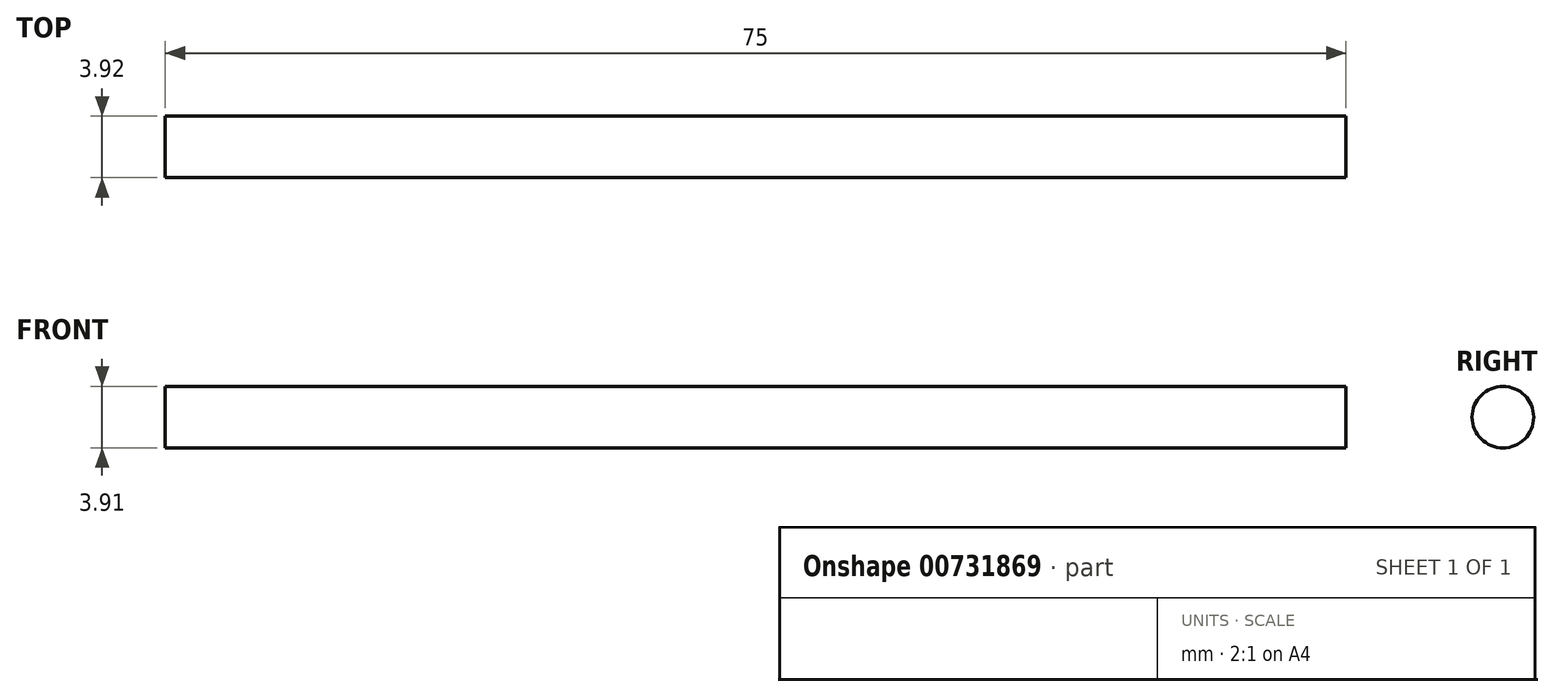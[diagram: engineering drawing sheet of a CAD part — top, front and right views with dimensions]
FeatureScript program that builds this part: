
annotation { "Feature Type Name" : "Feature", "Feature Type Description" : "" }
export const myFeature = defineFeature(function(context is Context, id is Id, definition is map)
    precondition{}
    {
        {
            var Q0;
            Q0=qCreatedBy(makeId("Right.planeOp"),FACE);
            var sketch = newSketch(context, id + "F0", { "sketchPlane" : qUnion([Q0])});
            skCircle(sketch, "E0", {"center": v(-4.15, 6.52) * mm, "radius": 1.96 * mm});
            skSolve(sketch);
        }
        {
            var Q0;
            Q0 = qSketchRegion(id + "F0", true);
            extrude(context, id + "F1", {"entities" : qUnion([Q0]), "depth" : 75 * mm, "offsetDistance" : 25 * mm});
        }
    });
